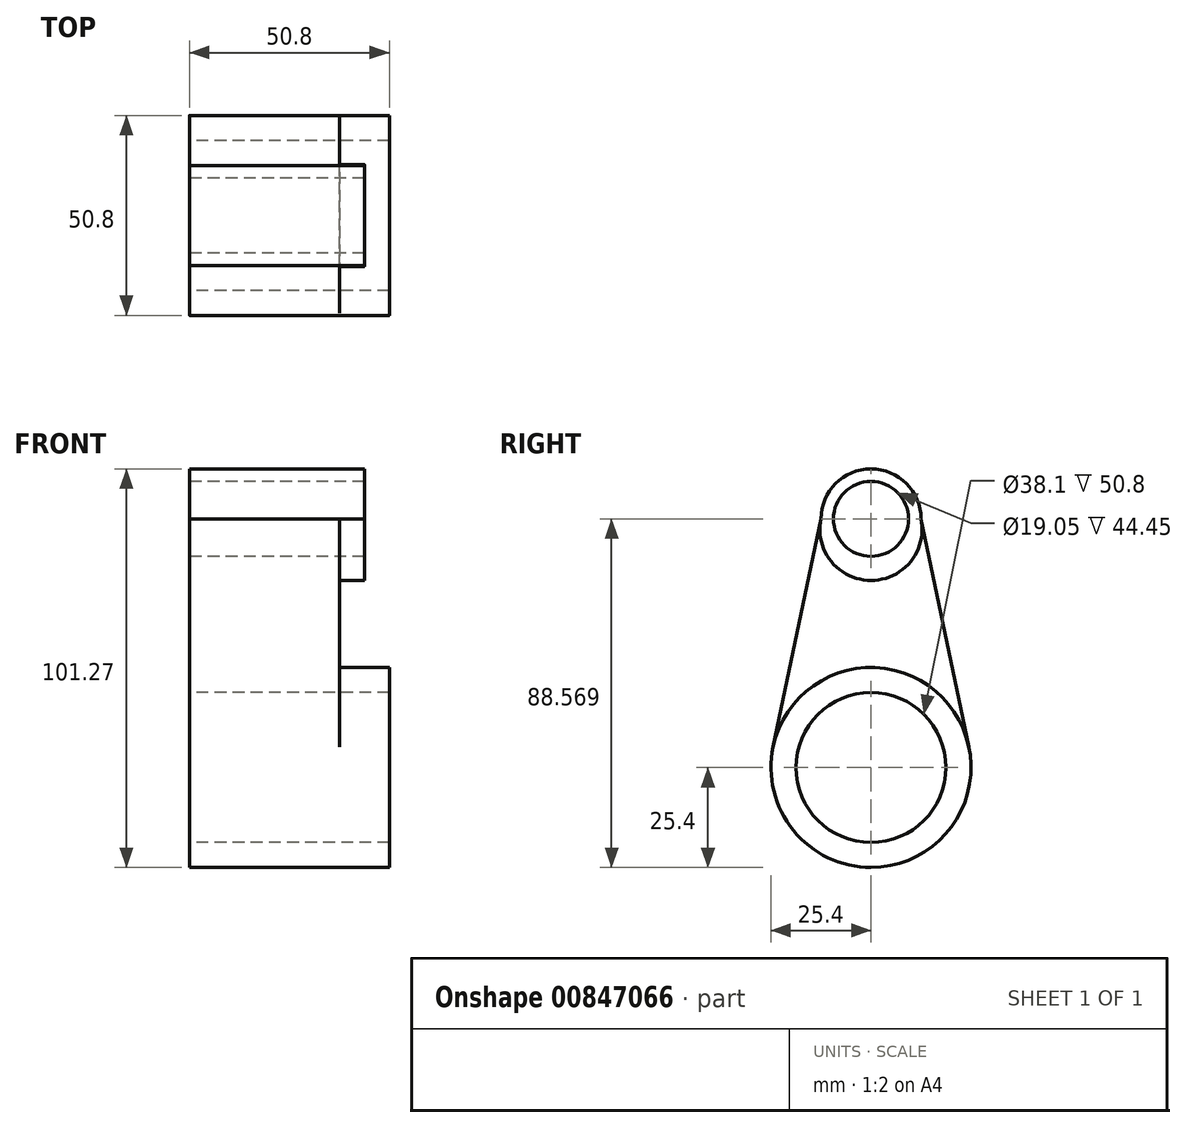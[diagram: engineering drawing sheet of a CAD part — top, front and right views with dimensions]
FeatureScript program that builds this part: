
annotation { "Feature Type Name" : "Feature", "Feature Type Description" : "" }
export const myFeature = defineFeature(function(context is Context, id is Id, definition is map)
    precondition{}
    {
        {
            var Q0;
            Q0=qCreatedBy(makeId("Right.planeOp"),FACE);
            var sketch = newSketch(context, id + "F0", { "sketchPlane" : qUnion([Q0])});
            skCircle(sketch, "E0", {"center": v(0, 0) * mm, "radius": 25.4 * mm});
            skCircle(sketch, "E1", {"center": v(0, 63.17) * mm, "radius": 12.7 * mm});
            skLineSegment(sketch, "E2", {"start": v(-12.7, 63.17) * mm, "end": v(-25.95, 0) * mm});
            skLineSegment(sketch, "E3", {"start": v(12.7, 63.17) * mm, "end": v(25.95, 0) * mm});
            skCircle(sketch, "E4", {"center": v(0, 0) * mm, "radius": 19.05 * mm});
            skCircle(sketch, "E5", {"center": v(0, 63.17) * mm, "radius": 9.53 * mm});
            skSolve(sketch);
        }
        {
            var Q0;
            {var subQ0=sQuery(id+"F0.wireOp",EDGE,"E0");var subQ1=makeQuery(id+"F0.imprint","INTERSECT",VERTEX,{"derivedFrom":[subQ0,sQuery(id+"F0.wireOp",EDGE,"E2")]});Q0=makeQuery(id+"F0.imprint","IMPRINT",FACE,{"disambiguationData":[TD([[makeQuery(id+"F0.imprint","IMPRINT",EDGE,{"disambiguationData":[TD([[subQ1,1.0]])],"derivedFrom":subQ0}),1.0]])]});}
            extrude(context, id + "F1", {"entities" : qUnion([Q0]), "depth" : 50.8 * mm, "offsetDistance" : 25.4 * mm});
        }
        {
            var Q0;
            {var subQ0=sQuery(id+"F0.wireOp",EDGE,"E2");var subQ1=sQuery(id+"F0.wireOp",EDGE,"E0");var subQ2=makeQuery(id+"F0.imprint","INTERSECT",VERTEX,{"derivedFrom":[subQ1,subQ0]});Q0=makeQuery(id+"F0.imprint","IMPRINT",FACE,{"disambiguationData":[TD([[makeQuery(id+"F0.imprint","IMPRINT",EDGE,{"disambiguationData":[TD([[subQ2,1.0]])],"derivedFrom":subQ1}),-1.0]])]});}
            extrude(context, id + "F2", {"entities" : qUnion([Q0]), "operationType" : NewBodyOperationType.ADD, "depth" : 44.45 * mm, "offsetDistance" : 25.4 * mm});
        }
        {
            var Q0;
            {var subQ0=sQuery(id+"F0.wireOp",EDGE,"E1");var subQ1=makeQuery(id+"F0.imprint","INTERSECT",VERTEX,{"derivedFrom":[subQ0,sQuery(id+"F0.wireOp",EDGE,"E2")]});Q0=makeQuery(id+"F0.imprint","IMPRINT",FACE,{"disambiguationData":[TD([[makeQuery(id+"F0.imprint","IMPRINT",EDGE,{"disambiguationData":[TD([[subQ1,1.0]])],"derivedFrom":subQ0}),1.0]])]});}
            extrude(context, id + "F3", {"entities" : qUnion([Q0]), "operationType" : NewBodyOperationType.ADD, "depth" : 44.45 * mm, "offsetDistance" : 25.4 * mm});
        }
        {
            var Q0;
            {var subQ0=sQuery(id+"F0.wireOp",EDGE,"E1");Q0=makeQuery(id+"F3.boolean.opBoolean","MERGE",FACE,{"derivedFrom":[makeQuery(id+"F2.opExtrude","CAP_FACE",FACE,{"disambiguationData":[OSD([sQuery(id+"F0.wireOp",EDGE,"E0"),subQ0,sQuery(id+"F0.wireOp",EDGE,"E2"),sQuery(id+"F0.wireOp",EDGE,"E3")])],"isStart":false}),makeQuery(id+"F3.opExtrude","CAP_FACE",FACE,{"disambiguationData":[OSD([subQ0,sQuery(id+"F0.wireOp",EDGE,"E5")])],"isStart":false})]});}
            var sketch = newSketch(context, id + "F4", { "sketchPlane" : qUnion([Q0])});
            skArc(sketch, "E6", {"start": v(24.86, 5.22) * mm, "mid": v(1.93, 25.33) * mm, "end": v(-23.78, 8.93) * mm});
            skArc(sketch, "E7", {"start": v(-12.7, 63.17) * mm, "mid": v(0, 47.53) * mm, "end": v(12.7, 63.17) * mm});
            skSolve(sketch);
        }
        {
            var Q0;
            {var subQ1=sQuery(id+"F4.wireOp",EDGE,"E6");Q0=makeQuery(id+"F4.imprint","IMPRINT",FACE,{"disambiguationData":[TD([[makeQuery(id+"F4.imprint","IMPRINT",EDGE,{"derivedFrom":subQ1}),-1.0]])]});}
            extrude(context, id + "F5", {"entities" : qUnion([Q0]), "operationType" : NewBodyOperationType.REMOVE, "oppositeDirection" : true, "depth" : 6.35 * mm, "offsetDistance" : 25.4 * mm});
        }
    });
